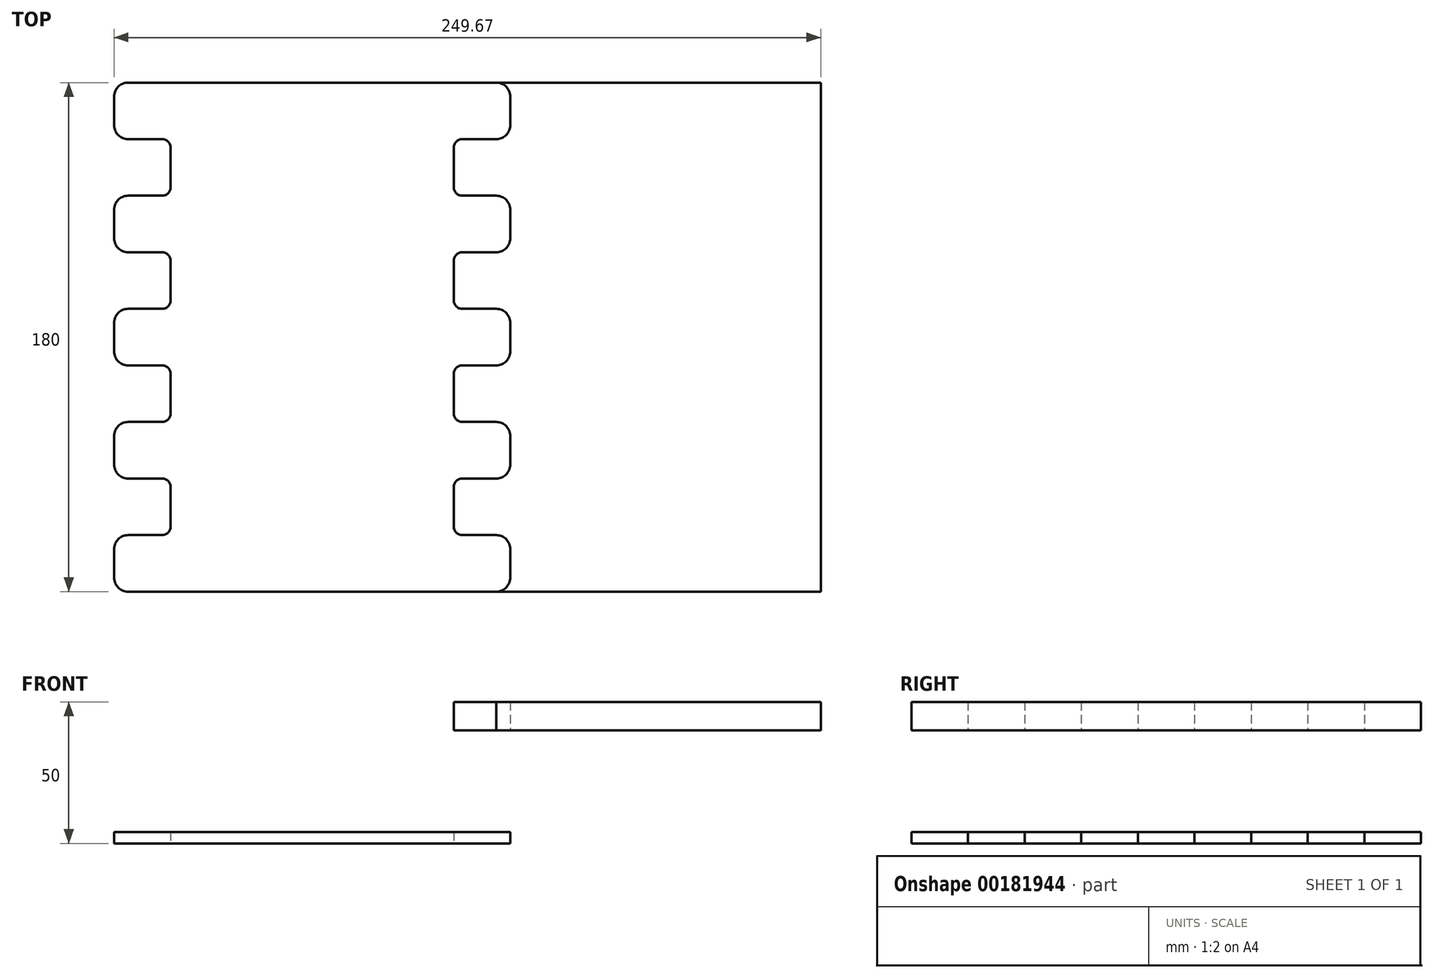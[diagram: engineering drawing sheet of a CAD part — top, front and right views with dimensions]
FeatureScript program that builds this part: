
annotation { "Feature Type Name" : "Feature", "Feature Type Description" : "" }
export const myFeature = defineFeature(function(context is Context, id is Id, definition is map)
    precondition{}
    {
        {
            var Q0;
            Q0=qCreatedBy(makeId("Top.planeOp"),FACE);
            var sketch = newSketch(context, id + "F0", { "sketchPlane" : qUnion([Q0])});
            skLineSegment(sketch, "E0.bottom", {"start": v(0, 0) * mm, "end": v(100, 0) * mm});
            skLineSegment(sketch, "E0.top", {"start": v(0, 180) * mm, "end": v(100, 180) * mm});
            skLineSegment(sketch, "E1.bottom", {"start": v(100, 0) * mm, "end": v(115, 0) * mm});
            skLineSegment(sketch, "E1.top", {"start": v(103, 20) * mm, "end": v(115, 20) * mm});
            skLineSegment(sketch, "E1.right", {"start": v(120, 5) * mm, "end": v(120, 15) * mm});
            skLineSegment(sketch, "E2", {"start": v(100, 23) * mm, "end": v(100, 37) * mm});
            skPoint(sketch, "E3.visualSharp", {"position": v(100, 40) * mm});
            skArc(sketch, "E3.filletArc", {"start": v(103, 40) * mm, "mid": v(100.88, 39.12) * mm, "end": v(100, 37) * mm});
            skPoint(sketch, "E4.visualSharp", {"position": v(100, 20) * mm});
            skArc(sketch, "E4.filletArc", {"start": v(100, 23) * mm, "mid": v(100.88, 20.88) * mm, "end": v(103, 20) * mm});
            skPoint(sketch, "E5.visualSharp", {"position": v(120, 20) * mm});
            skArc(sketch, "E5.filletArc", {"start": v(120, 15) * mm, "mid": v(118.54, 18.54) * mm, "end": v(115, 20) * mm});
            skPoint(sketch, "E6.visualSharp", {"position": v(120, 0) * mm});
            skArc(sketch, "E6.filletArc", {"start": v(115, 0) * mm, "mid": v(118.54, 1.46) * mm, "end": v(120, 5) * mm});
            skLineSegment(sketch, "E7", {"start": v(50, -57.47) * mm, "end": v(50, -101.97) * mm, "construction": true});
            skPoint(sketch, "E7.startSnap0", {"position": v(50, 0) * mm});
            skLineSegment(sketch, "E8.MirrorCS", {"start": v(0, 0) * mm, "end": v(-15, 0) * mm});
            skArc(sketch, "E9.MirrorCS", {"start": v(-15, 0) * mm, "mid": v(-18.54, 1.46) * mm, "end": v(-20, 5) * mm});
            skPoint(sketch, "E10.MirrorP", {"position": v(-20, 0) * mm});
            skLineSegment(sketch, "E11.MirrorCS", {"start": v(-20, 5) * mm, "end": v(-20, 15) * mm});
            skArc(sketch, "E12.MirrorCS", {"start": v(-20, 15) * mm, "mid": v(-18.54, 18.54) * mm, "end": v(-15, 20) * mm});
            skPoint(sketch, "E13.MirrorP", {"position": v(-20, 20) * mm});
            skLineSegment(sketch, "E14.MirrorCS", {"start": v(-3, 20) * mm, "end": v(-15, 20) * mm});
            skArc(sketch, "E15.MirrorCS", {"start": v(0, 23) * mm, "mid": v(-0.88, 20.88) * mm, "end": v(-3, 20) * mm});
            skPoint(sketch, "E16.MirrorP", {"position": v(0, 20) * mm});
            skArc(sketch, "E17.MirrorCS", {"start": v(-3, 40) * mm, "mid": v(-0.88, 39.12) * mm, "end": v(0, 37) * mm});
            skPoint(sketch, "E18.MirrorP", {"position": v(0, 40) * mm});
            skLineSegment(sketch, "E19.MirrorCS", {"start": v(0, 23) * mm, "end": v(0, 37) * mm});
            skLineSegment(sketch, "E20.0.1.0", {"start": v(0, 40) * mm, "end": v(-15, 40) * mm});
            skLineSegment(sketch, "E20.0.1.1", {"start": v(-3, 60) * mm, "end": v(-15, 60) * mm});
            skLineSegment(sketch, "E20.0.1.2", {"start": v(100, 40) * mm, "end": v(115, 40) * mm});
            skLineSegment(sketch, "E20.0.1.3", {"start": v(103, 60) * mm, "end": v(115, 60) * mm});
            skLineSegment(sketch, "E20.0.1.4", {"start": v(100, 63) * mm, "end": v(100, 77) * mm});
            skArc(sketch, "E20.0.1.5", {"start": v(103, 80) * mm, "mid": v(100.88, 79.12) * mm, "end": v(100, 77) * mm});
            skPoint(sketch, "E20.0.1.6", {"position": v(100, 80) * mm});
            skPoint(sketch, "E20.0.1.7", {"position": v(100, 60) * mm});
            skArc(sketch, "E20.0.1.8", {"start": v(100, 63) * mm, "mid": v(100.88, 60.88) * mm, "end": v(103, 60) * mm});
            skArc(sketch, "E20.0.1.9", {"start": v(115, 40) * mm, "mid": v(118.54, 41.46) * mm, "end": v(120, 45) * mm});
            skLineSegment(sketch, "E20.0.1.10", {"start": v(120, 45) * mm, "end": v(120, 55) * mm});
            skArc(sketch, "E20.0.1.11", {"start": v(120, 55) * mm, "mid": v(118.54, 58.54) * mm, "end": v(115, 60) * mm});
            skPoint(sketch, "E20.0.1.12", {"position": v(120, 60) * mm});
            skPoint(sketch, "E20.0.1.13", {"position": v(120, 40) * mm});
            skLineSegment(sketch, "E20.0.1.14", {"start": v(-20, 45) * mm, "end": v(-20, 55) * mm});
            skArc(sketch, "E20.0.1.15", {"start": v(-15, 40) * mm, "mid": v(-18.54, 41.46) * mm, "end": v(-20, 45) * mm});
            skPoint(sketch, "E20.0.1.16", {"position": v(-20, 40) * mm});
            skArc(sketch, "E20.0.1.17", {"start": v(-20, 55) * mm, "mid": v(-18.54, 58.54) * mm, "end": v(-15, 60) * mm});
            skPoint(sketch, "E20.0.1.18", {"position": v(-20, 60) * mm});
            skPoint(sketch, "E20.0.1.19", {"position": v(0, 60) * mm});
            skArc(sketch, "E20.0.1.20", {"start": v(0, 63) * mm, "mid": v(-0.88, 60.88) * mm, "end": v(-3, 60) * mm});
            skLineSegment(sketch, "E20.0.1.21", {"start": v(0, 63) * mm, "end": v(0, 77) * mm});
            skArc(sketch, "E20.0.1.22", {"start": v(-3, 80) * mm, "mid": v(-0.88, 79.12) * mm, "end": v(0, 77) * mm});
            skLineSegment(sketch, "E20.0.2.0", {"start": v(0, 80) * mm, "end": v(-15, 80) * mm});
            skLineSegment(sketch, "E20.0.2.1", {"start": v(-3, 100) * mm, "end": v(-15, 100) * mm});
            skLineSegment(sketch, "E20.0.2.2", {"start": v(100, 80) * mm, "end": v(115, 80) * mm});
            skLineSegment(sketch, "E20.0.2.3", {"start": v(103, 100) * mm, "end": v(115, 100) * mm});
            skLineSegment(sketch, "E20.0.2.4", {"start": v(100, 103) * mm, "end": v(100, 117) * mm});
            skArc(sketch, "E20.0.2.5", {"start": v(103, 120) * mm, "mid": v(100.88, 119.12) * mm, "end": v(100, 117) * mm});
            skPoint(sketch, "E20.0.2.6", {"position": v(100, 120) * mm});
            skPoint(sketch, "E20.0.2.7", {"position": v(100, 100) * mm});
            skArc(sketch, "E20.0.2.8", {"start": v(100, 103) * mm, "mid": v(100.88, 100.88) * mm, "end": v(103, 100) * mm});
            skArc(sketch, "E20.0.2.9", {"start": v(115, 80) * mm, "mid": v(118.54, 81.46) * mm, "end": v(120, 85) * mm});
            skLineSegment(sketch, "E20.0.2.10", {"start": v(120, 85) * mm, "end": v(120, 95) * mm});
            skArc(sketch, "E20.0.2.11", {"start": v(120, 95) * mm, "mid": v(118.54, 98.54) * mm, "end": v(115, 100) * mm});
            skPoint(sketch, "E20.0.2.12", {"position": v(120, 100) * mm});
            skPoint(sketch, "E20.0.2.13", {"position": v(120, 80) * mm});
            skLineSegment(sketch, "E20.0.2.14", {"start": v(-20, 85) * mm, "end": v(-20, 95) * mm});
            skArc(sketch, "E20.0.2.15", {"start": v(-15, 80) * mm, "mid": v(-18.54, 81.46) * mm, "end": v(-20, 85) * mm});
            skPoint(sketch, "E20.0.2.16", {"position": v(-20, 80) * mm});
            skArc(sketch, "E20.0.2.17", {"start": v(-20, 95) * mm, "mid": v(-18.54, 98.54) * mm, "end": v(-15, 100) * mm});
            skPoint(sketch, "E20.0.2.18", {"position": v(-20, 100) * mm});
            skPoint(sketch, "E20.0.2.19", {"position": v(0, 100) * mm});
            skArc(sketch, "E20.0.2.20", {"start": v(0, 103) * mm, "mid": v(-0.88, 100.88) * mm, "end": v(-3, 100) * mm});
            skLineSegment(sketch, "E20.0.2.21", {"start": v(0, 103) * mm, "end": v(0, 117) * mm});
            skArc(sketch, "E20.0.2.22", {"start": v(-3, 120) * mm, "mid": v(-0.88, 119.12) * mm, "end": v(0, 117) * mm});
            skLineSegment(sketch, "E20.0.3.0", {"start": v(0, 120) * mm, "end": v(-15, 120) * mm});
            skLineSegment(sketch, "E20.0.3.1", {"start": v(-3, 140) * mm, "end": v(-15, 140) * mm});
            skLineSegment(sketch, "E20.0.3.2", {"start": v(100, 120) * mm, "end": v(115, 120) * mm});
            skLineSegment(sketch, "E20.0.3.3", {"start": v(103, 140) * mm, "end": v(115, 140) * mm});
            skLineSegment(sketch, "E20.0.3.4", {"start": v(100, 143) * mm, "end": v(100, 157) * mm});
            skArc(sketch, "E20.0.3.5", {"start": v(103, 160) * mm, "mid": v(100.88, 159.12) * mm, "end": v(100, 157) * mm});
            skPoint(sketch, "E20.0.3.6", {"position": v(100, 160) * mm});
            skPoint(sketch, "E20.0.3.7", {"position": v(100, 140) * mm});
            skArc(sketch, "E20.0.3.8", {"start": v(100, 143) * mm, "mid": v(100.88, 140.88) * mm, "end": v(103, 140) * mm});
            skArc(sketch, "E20.0.3.9", {"start": v(115, 120) * mm, "mid": v(118.54, 121.46) * mm, "end": v(120, 125) * mm});
            skLineSegment(sketch, "E20.0.3.10", {"start": v(120, 125) * mm, "end": v(120, 135) * mm});
            skArc(sketch, "E20.0.3.11", {"start": v(120, 135) * mm, "mid": v(118.54, 138.54) * mm, "end": v(115, 140) * mm});
            skPoint(sketch, "E20.0.3.12", {"position": v(120, 140) * mm});
            skPoint(sketch, "E20.0.3.13", {"position": v(120, 120) * mm});
            skLineSegment(sketch, "E20.0.3.14", {"start": v(-20, 125) * mm, "end": v(-20, 135) * mm});
            skArc(sketch, "E20.0.3.15", {"start": v(-15, 120) * mm, "mid": v(-18.54, 121.46) * mm, "end": v(-20, 125) * mm});
            skPoint(sketch, "E20.0.3.16", {"position": v(-20, 120) * mm});
            skArc(sketch, "E20.0.3.17", {"start": v(-20, 135) * mm, "mid": v(-18.54, 138.54) * mm, "end": v(-15, 140) * mm});
            skPoint(sketch, "E20.0.3.18", {"position": v(-20, 140) * mm});
            skPoint(sketch, "E20.0.3.19", {"position": v(0, 140) * mm});
            skArc(sketch, "E20.0.3.20", {"start": v(0, 143) * mm, "mid": v(-0.88, 140.88) * mm, "end": v(-3, 140) * mm});
            skLineSegment(sketch, "E20.0.3.21", {"start": v(0, 143) * mm, "end": v(0, 157) * mm});
            skArc(sketch, "E20.0.3.22", {"start": v(-3, 160) * mm, "mid": v(-0.88, 159.12) * mm, "end": v(0, 157) * mm});
            skLineSegment(sketch, "E20.0.4.0", {"start": v(0, 160) * mm, "end": v(-15, 160) * mm});
            skLineSegment(sketch, "E20.0.4.2", {"start": v(100, 160) * mm, "end": v(115, 160) * mm});
            skPoint(sketch, "E20.0.4.7", {"position": v(100, 180) * mm});
            skArc(sketch, "E20.0.4.9", {"start": v(115, 160) * mm, "mid": v(118.54, 161.46) * mm, "end": v(120, 165) * mm});
            skLineSegment(sketch, "E20.0.4.10", {"start": v(120, 165) * mm, "end": v(120, 175) * mm});
            skArc(sketch, "E20.0.4.11", {"start": v(120, 175) * mm, "mid": v(118.54, 178.54) * mm, "end": v(115, 180) * mm});
            skPoint(sketch, "E20.0.4.12", {"position": v(120, 180) * mm});
            skPoint(sketch, "E20.0.4.13", {"position": v(120, 160) * mm});
            skLineSegment(sketch, "E20.0.4.14", {"start": v(-20, 165) * mm, "end": v(-20, 175) * mm});
            skArc(sketch, "E20.0.4.15", {"start": v(-15, 160) * mm, "mid": v(-18.54, 161.46) * mm, "end": v(-20, 165) * mm});
            skPoint(sketch, "E20.0.4.16", {"position": v(-20, 160) * mm});
            skArc(sketch, "E20.0.4.17", {"start": v(-20, 175) * mm, "mid": v(-18.54, 178.54) * mm, "end": v(-15, 180) * mm});
            skPoint(sketch, "E20.0.4.18", {"position": v(-20, 180) * mm});
            skPoint(sketch, "E20.0.4.19", {"position": v(0, 180) * mm});
            skLineSegment(sketch, "E20.direction1", {"start": v(-15, 0) * mm, "end": v(10, 0) * mm, "construction": true});
            skLineSegment(sketch, "E20.direction2", {"start": v(-15, 0) * mm, "end": v(-15, 40) * mm, "construction": true});
            skLineSegment(sketch, "E21", {"start": v(-15, 180) * mm, "end": v(115, 180) * mm});
            skLineSegment(sketch, "E22", {"start": v(115, 180) * mm, "end": v(229.67, 180) * mm});
            skLineSegment(sketch, "E23", {"start": v(229.67, 180) * mm, "end": v(229.67, 0) * mm});
            skPoint(sketch, "E23.endSnap0", {"position": v(107.5, 0) * mm});
            skLineSegment(sketch, "E24", {"start": v(229.67, 0) * mm, "end": v(100, 0) * mm});
            skSolve(sketch);
        }
        {
            var Q0;
            Q0=makeQuery(id+"F0.imprint","IMPRINT",FACE,{"disambiguationData":[TD([[makeQuery(id+"F0.imprint","IMPRINT",EDGE,{"derivedFrom":sQuery(id+"F0.wireOp",EDGE,"E0.bottom")}),1.0]])]});
            extrude(context, id + "F1", {"entities" : qUnion([Q0]), "depth" : 4 * mm});
        }
        {
            var Q0;
            Q0=makeQuery(id+"F0.imprint","IMPRINT",FACE,{"disambiguationData":[TD([[makeQuery(id+"F0.imprint","IMPRINT",EDGE,{"derivedFrom":sQuery(id+"F0.wireOp",EDGE,"E1.top")}),1.0]])]});
            extrude(context, id + "F2", {"entities" : qUnion([Q0]), "depth" : 50 * mm, "hasSecondDirection" : true, "secondDirectionOppositeDirection" : false, "secondDirectionDepth" : 40 * mm});
        }
    });
